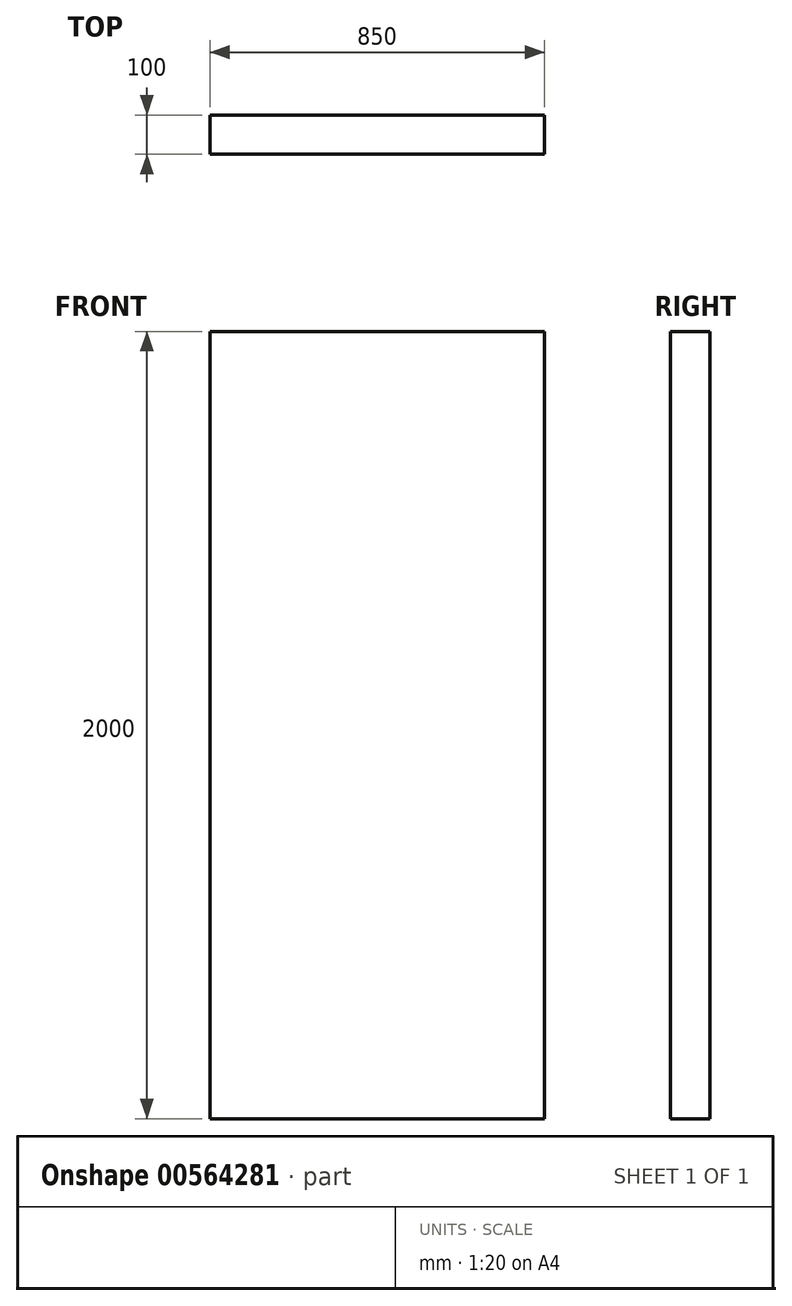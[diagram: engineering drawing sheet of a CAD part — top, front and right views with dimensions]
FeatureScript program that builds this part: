
annotation { "Feature Type Name" : "Feature", "Feature Type Description" : "" }
export const myFeature = defineFeature(function(context is Context, id is Id, definition is map)
    precondition{}
    {
        {
            var Q0;
            Q0=qCreatedBy(makeId("Front.planeOp"),FACE);
            var sketch = newSketch(context, id + "F0", { "sketchPlane" : qUnion([Q0])});
            skLineSegment(sketch, "E0.bottom", {"start": v(-433.75, 999.1) * mm, "end": v(416.25, 999.1) * mm});
            skLineSegment(sketch, "E0.top", {"start": v(-433.75, -1000.9) * mm, "end": v(416.25, -1000.9) * mm});
            skLineSegment(sketch, "E0.left", {"start": v(-433.75, 999.1) * mm, "end": v(-433.75, -1000.9) * mm});
            skLineSegment(sketch, "E0.right", {"start": v(416.25, 999.1) * mm, "end": v(416.25, -1000.9) * mm});
            skSolve(sketch);
        }
        {
            var Q0;
            Q0=makeQuery(id+"F0.imprint","IMPRINT",FACE,{"disambiguationData":[TD([[makeQuery(id+"F0.imprint","IMPRINT",EDGE,{"derivedFrom":sQuery(id+"F0.wireOp",EDGE,"E0.bottom")}),-1.0]])]});
            extrude(context, id + "F1", {"entities" : qUnion([Q0]), "depth" : 100 * mm, "offsetDistance" : 25 * mm});
        }
    });
